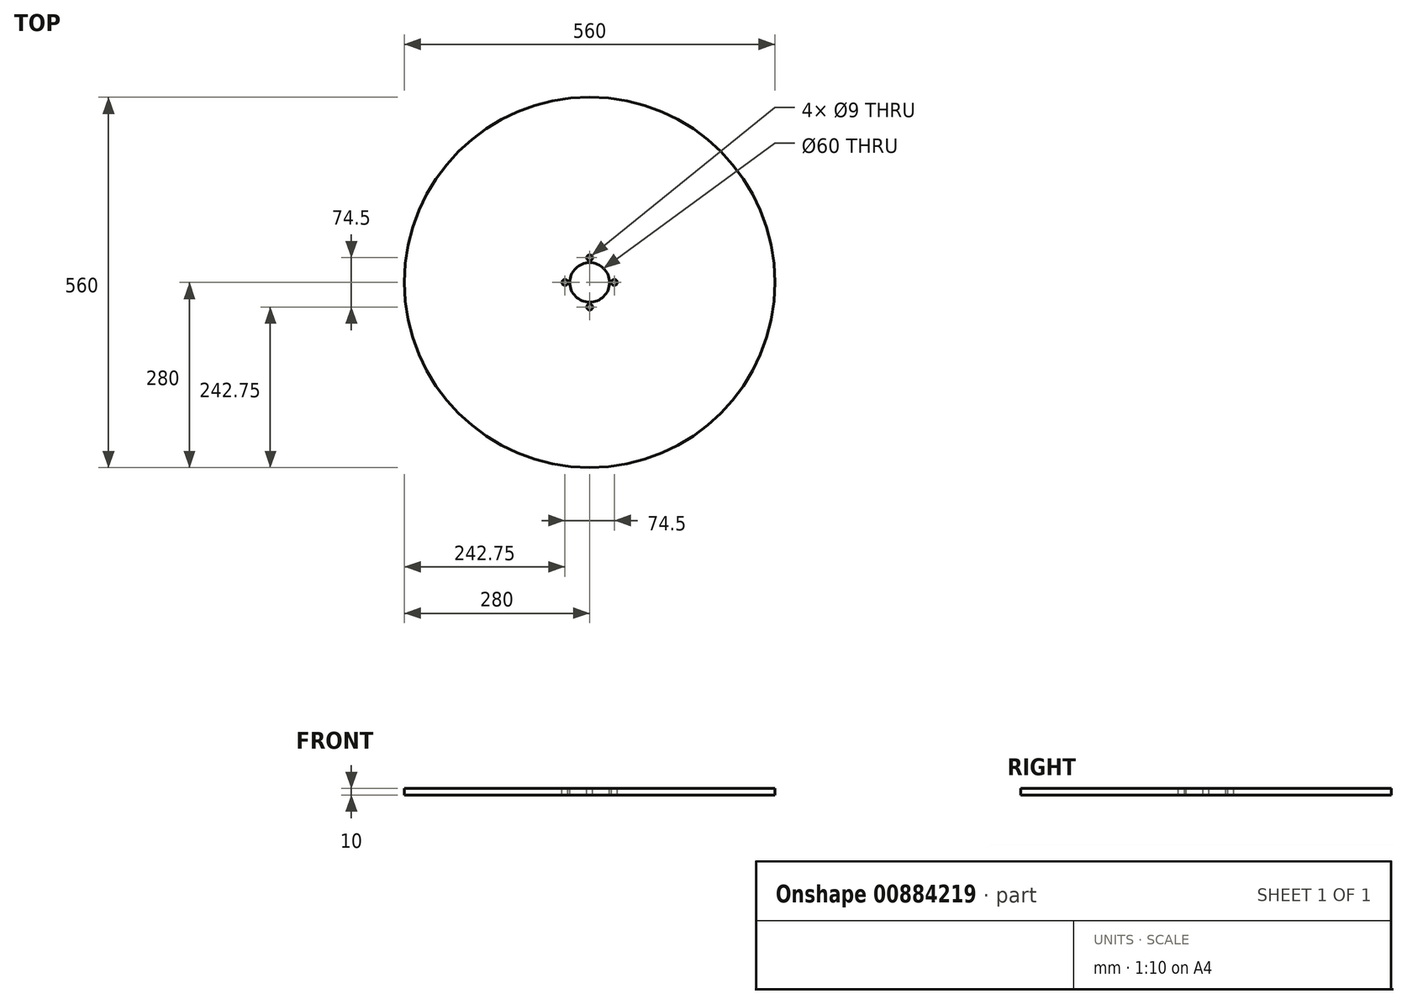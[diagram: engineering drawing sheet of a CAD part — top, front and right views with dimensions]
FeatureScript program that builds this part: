
annotation { "Feature Type Name" : "Feature", "Feature Type Description" : "" }
export const myFeature = defineFeature(function(context is Context, id is Id, definition is map)
    precondition{}
    {
        {
            var Q0;
            Q0=qCreatedBy(makeId("Top.planeOp"),FACE);
            var sketch = newSketch(context, id + "F0", { "sketchPlane" : qUnion([Q0])});
            skCircle(sketch, "E0", {"center": v(0, 0) * mm, "radius": 280 * mm});
            skSolve(sketch);
        }
        {
            var Q0;
            Q0=makeQuery(id+"F0.imprint","IMPRINT",FACE,{"disambiguationData":[TD([[makeQuery(id+"F0.imprint","IMPRINT",EDGE,{"derivedFrom":sQuery(id+"F0.wireOp",EDGE,"E0")}),1.0]])]});
            extrude(context, id + "F1", {"entities" : qUnion([Q0]), "depth" : 10 * mm, "offsetDistance" : 25 * mm});
        }
        {
            var Q0;
            Q0=makeQuery(id+"F1.opExtrude","CAP_FACE",FACE,{"disambiguationData":[OSD([sQuery(id+"F0.wireOp",EDGE,"E0")])],"isStart":false});
            var sketch = newSketch(context, id + "F2", { "sketchPlane" : qUnion([Q0])});
            skCircle(sketch, "E1", {"center": v(0, 0) * mm, "radius": 30 * mm});
            skCircle(sketch, "E2", {"center": v(0, 0) * mm, "radius": 37.25 * mm, "construction": true});
            skCircle(sketch, "E3", {"center": v(0, 37.25) * mm, "radius": 4.5 * mm});
            skCircle(sketch, "E4", {"center": v(-37.25, 0) * mm, "radius": 4.5 * mm});
            skCircle(sketch, "E5", {"center": v(37.25, 0) * mm, "radius": 4.5 * mm});
            skCircle(sketch, "E6", {"center": v(0, -37.25) * mm, "radius": 4.5 * mm});
            skSolve(sketch);
        }
        {
            var Q0;
            Q0=makeQuery(id+"F2.imprint","IMPRINT",FACE,{"disambiguationData":[TD([[makeQuery(id+"F2.imprint","IMPRINT",EDGE,{"derivedFrom":sQuery(id+"F2.wireOp",EDGE,"E1")}),1.0]])]});
            var Q1;
            Q1=makeQuery(id+"F2.imprint","IMPRINT",FACE,{"disambiguationData":[TD([[makeQuery(id+"F2.imprint","IMPRINT",EDGE,{"derivedFrom":sQuery(id+"F2.wireOp",EDGE,"HDDMHsGB-oVZA-M6vI-Bz3S-lTRq8NOSrvcb")}),1.0]])]});
            var Q2;
            Q2=makeQuery(id+"F2.imprint","IMPRINT",FACE,{"disambiguationData":[TD([[makeQuery(id+"F2.imprint","IMPRINT",EDGE,{"derivedFrom":sQuery(id+"F2.wireOp",EDGE,"E4")}),1.0]])]});
            var Q3;
            Q3=makeQuery(id+"F2.imprint","IMPRINT",FACE,{"disambiguationData":[TD([[makeQuery(id+"F2.imprint","IMPRINT",EDGE,{"derivedFrom":sQuery(id+"F2.wireOp",EDGE,"E3")}),1.0]])]});
            var Q4;
            Q4=makeQuery(id+"F2.imprint","IMPRINT",FACE,{"disambiguationData":[TD([[makeQuery(id+"F2.imprint","IMPRINT",EDGE,{"derivedFrom":sQuery(id+"F2.wireOp",EDGE,"E5")}),1.0]])]});
            var Q5;
            Q5=makeQuery(id+"F2.imprint","IMPRINT",FACE,{"disambiguationData":[TD([[makeQuery(id+"F2.imprint","IMPRINT",EDGE,{"derivedFrom":sQuery(id+"F2.wireOp",EDGE,"E6")}),1.0]])]});
            extrude(context, id + "F3", {"entities" : qUnion([Q0, Q1, Q2, Q3, Q4, Q5]), "operationType" : NewBodyOperationType.REMOVE, "oppositeDirection" : true, "depth" : 25 * mm, "offsetDistance" : 25 * mm});
        }
    });
